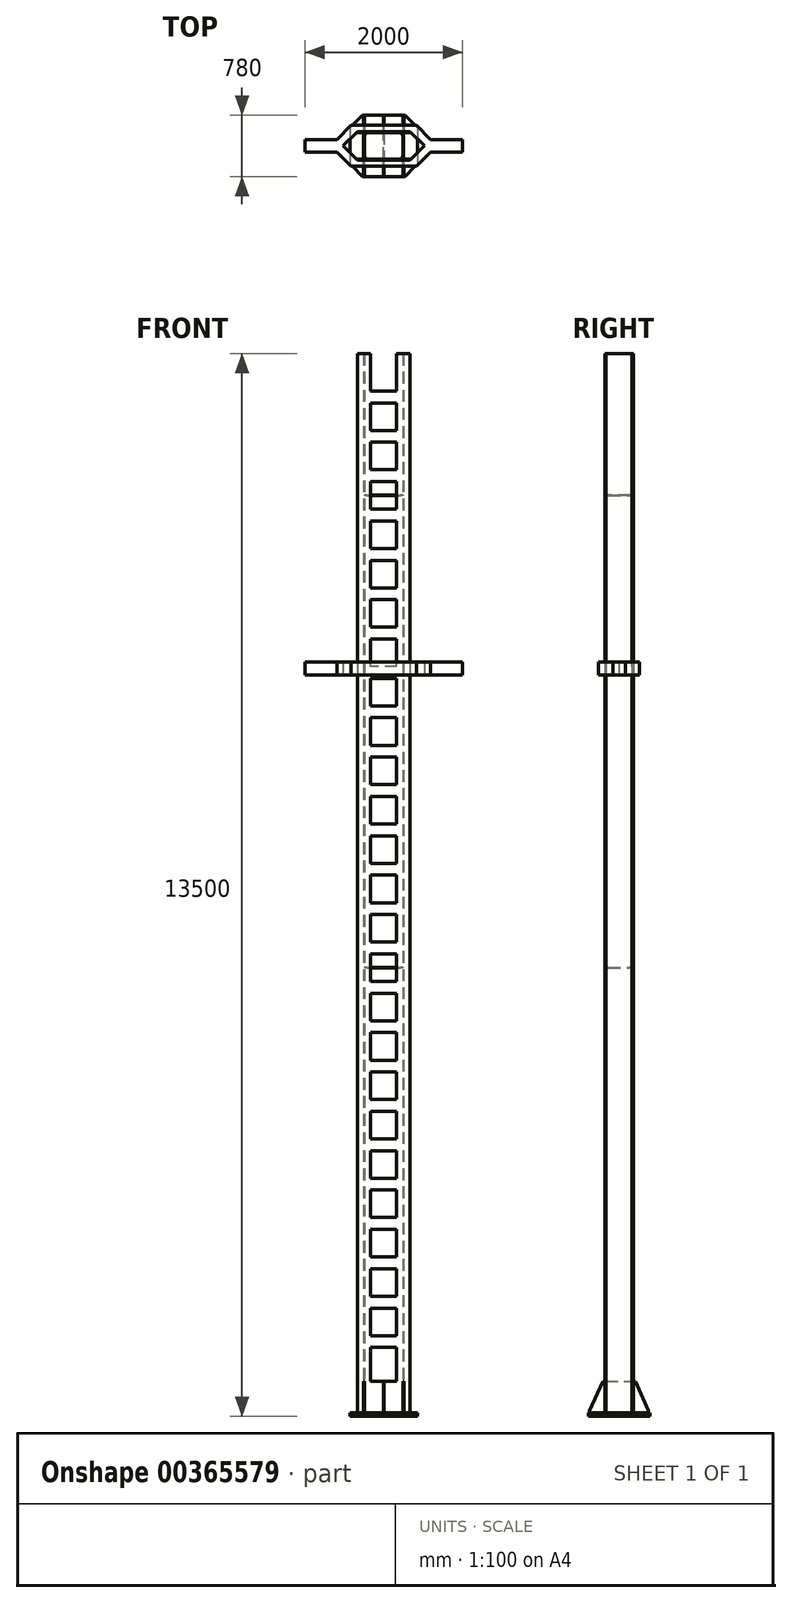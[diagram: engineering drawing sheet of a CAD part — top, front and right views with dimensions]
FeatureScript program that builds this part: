
annotation { "Feature Type Name" : "Feature", "Feature Type Description" : "" }
export const myFeature = defineFeature(function(context is Context, id is Id, definition is map)
    precondition{}
    {
        {
            var Q0;
            Q0=qCreatedBy(makeId("Top.planeOp"),FACE);
            var sketch = newSketch(context, id + "F0", { "sketchPlane" : qUnion([Q0])});
            skLineSegment(sketch, "E0", {"start": v(-335, -180) * mm, "end": v(-335, -166) * mm});
            skLineSegment(sketch, "E1", {"start": v(-335, -166) * mm, "end": v(335, -166) * mm});
            skLineSegment(sketch, "E2", {"start": v(335, -166) * mm, "end": v(335, -180) * mm});
            skLineSegment(sketch, "E3", {"start": v(-335, 180) * mm, "end": v(-335, 166) * mm});
            skLineSegment(sketch, "E4", {"start": v(-335, 166) * mm, "end": v(335, 166) * mm});
            skLineSegment(sketch, "E5", {"start": v(335, 166) * mm, "end": v(335, 180) * mm});
            skLineSegment(sketch, "E6", {"start": v(-246, 166) * mm, "end": v(-246, -166) * mm});
            skLineSegment(sketch, "E7", {"start": v(246, 166) * mm, "end": v(246, -166) * mm});
            skLineSegment(sketch, "E8", {"start": v(-254, -166) * mm, "end": v(-254, 166) * mm});
            skLineSegment(sketch, "E9", {"start": v(254, -166) * mm, "end": v(254, 166) * mm});
            skLineSegment(sketch, "E10", {"start": v(-335, -180) * mm, "end": v(335, -180) * mm});
            skLineSegment(sketch, "E11", {"start": v(-335, 180) * mm, "end": v(335, 180) * mm});
            skSolve(sketch);
        }
        {
            var Q0;
            Q0 = qSketchRegion(id + "F0", true);
            var Q1;
            Q1 = qConstructionFilter(qBodyType(qCreatedBy(id + "F0" ,EDGE), BodyType.WIRE), ConstructionObject.NO);
            extrude(context, id + "F1", {"entities" : qUnion([Q0]), "surfaceEntities" : qUnion([Q1]), "depth" : 13500 * mm});
        }
        {
            var Q0;
            Q0=makeQuery(id+"F1.opExtrude","SWEPT_FACE",FACE,{"disambiguationData":[OSD([sQuery(id+"F0.wireOp",EDGE,"E10")])]});
            var sketch = newSketch(context, id + "F2", { "sketchPlane" : qUnion([Q0])});
            skLineSegment(sketch, "E12.bottom", {"start": v(-165, 13500) * mm, "end": v(165, 13500) * mm});
            skLineSegment(sketch, "E12.top", {"start": v(-165, 13025) * mm, "end": v(165, 13025) * mm});
            skLineSegment(sketch, "E12.left", {"start": v(-165, 13500) * mm, "end": v(-165, 13025) * mm});
            skLineSegment(sketch, "E12.right", {"start": v(165, 13500) * mm, "end": v(165, 13025) * mm});
            skLineSegment(sketch, "E13.bottom", {"start": v(-165, 12875) * mm, "end": v(165, 12875) * mm});
            skLineSegment(sketch, "E13.top", {"start": v(-165, 12525) * mm, "end": v(165, 12525) * mm});
            skLineSegment(sketch, "E13.left", {"start": v(-165, 12875) * mm, "end": v(-165, 12525) * mm});
            skLineSegment(sketch, "E13.right", {"start": v(165, 12875) * mm, "end": v(165, 12525) * mm});
            skLineSegment(sketch, "E14.0.1.0", {"start": v(-165, 12025) * mm, "end": v(165, 12025) * mm});
            skLineSegment(sketch, "E14.0.1.1", {"start": v(165, 12375) * mm, "end": v(165, 12025) * mm});
            skLineSegment(sketch, "E14.0.1.2", {"start": v(-165, 12375) * mm, "end": v(-165, 12025) * mm});
            skLineSegment(sketch, "E14.0.1.3", {"start": v(-165, 12375) * mm, "end": v(165, 12375) * mm});
            skLineSegment(sketch, "E14.0.2.0", {"start": v(-165, 11525) * mm, "end": v(165, 11525) * mm});
            skLineSegment(sketch, "E14.0.2.1", {"start": v(165, 11875) * mm, "end": v(165, 11525) * mm});
            skLineSegment(sketch, "E14.0.2.2", {"start": v(-165, 11875) * mm, "end": v(-165, 11525) * mm});
            skLineSegment(sketch, "E14.0.2.3", {"start": v(-165, 11875) * mm, "end": v(165, 11875) * mm});
            skLineSegment(sketch, "E14.0.3.0", {"start": v(-165, 11025) * mm, "end": v(165, 11025) * mm});
            skLineSegment(sketch, "E14.0.3.1", {"start": v(165, 11375) * mm, "end": v(165, 11025) * mm});
            skLineSegment(sketch, "E14.0.3.2", {"start": v(-165, 11375) * mm, "end": v(-165, 11025) * mm});
            skLineSegment(sketch, "E14.0.3.3", {"start": v(-165, 11375) * mm, "end": v(165, 11375) * mm});
            skLineSegment(sketch, "E14.0.4.0", {"start": v(-165, 10525) * mm, "end": v(165, 10525) * mm});
            skLineSegment(sketch, "E14.0.4.1", {"start": v(165, 10875) * mm, "end": v(165, 10525) * mm});
            skLineSegment(sketch, "E14.0.4.2", {"start": v(-165, 10875) * mm, "end": v(-165, 10525) * mm});
            skLineSegment(sketch, "E14.0.4.3", {"start": v(-165, 10875) * mm, "end": v(165, 10875) * mm});
            skLineSegment(sketch, "E14.0.5.0", {"start": v(-165, 10025) * mm, "end": v(165, 10025) * mm});
            skLineSegment(sketch, "E14.0.5.1", {"start": v(165, 10375) * mm, "end": v(165, 10025) * mm});
            skLineSegment(sketch, "E14.0.5.2", {"start": v(-165, 10375) * mm, "end": v(-165, 10025) * mm});
            skLineSegment(sketch, "E14.0.5.3", {"start": v(-165, 10375) * mm, "end": v(165, 10375) * mm});
            skLineSegment(sketch, "E14.0.6.0", {"start": v(-165, 9525) * mm, "end": v(165, 9525) * mm});
            skLineSegment(sketch, "E14.0.6.1", {"start": v(165, 9875) * mm, "end": v(165, 9525) * mm});
            skLineSegment(sketch, "E14.0.6.2", {"start": v(-165, 9875) * mm, "end": v(-165, 9525) * mm});
            skLineSegment(sketch, "E14.0.6.3", {"start": v(-165, 9875) * mm, "end": v(165, 9875) * mm});
            skLineSegment(sketch, "E14.0.7.0", {"start": v(-165, 9025) * mm, "end": v(165, 9025) * mm});
            skLineSegment(sketch, "E14.0.7.1", {"start": v(165, 9375) * mm, "end": v(165, 9025) * mm});
            skLineSegment(sketch, "E14.0.7.2", {"start": v(-165, 9375) * mm, "end": v(-165, 9025) * mm});
            skLineSegment(sketch, "E14.0.7.3", {"start": v(-165, 9375) * mm, "end": v(165, 9375) * mm});
            skLineSegment(sketch, "E14.0.8.0", {"start": v(-165, 8525) * mm, "end": v(165, 8525) * mm});
            skLineSegment(sketch, "E14.0.8.1", {"start": v(165, 8875) * mm, "end": v(165, 8525) * mm});
            skLineSegment(sketch, "E14.0.8.2", {"start": v(-165, 8875) * mm, "end": v(-165, 8525) * mm});
            skLineSegment(sketch, "E14.0.8.3", {"start": v(-165, 8875) * mm, "end": v(165, 8875) * mm});
            skLineSegment(sketch, "E14.0.9.0", {"start": v(-165, 8025) * mm, "end": v(165, 8025) * mm});
            skLineSegment(sketch, "E14.0.9.1", {"start": v(165, 8375) * mm, "end": v(165, 8025) * mm});
            skLineSegment(sketch, "E14.0.9.2", {"start": v(-165, 8375) * mm, "end": v(-165, 8025) * mm});
            skLineSegment(sketch, "E14.0.9.3", {"start": v(-165, 8375) * mm, "end": v(165, 8375) * mm});
            skLineSegment(sketch, "E14.0.10.0", {"start": v(-165, 7525) * mm, "end": v(165, 7525) * mm});
            skLineSegment(sketch, "E14.0.10.1", {"start": v(165, 7875) * mm, "end": v(165, 7525) * mm});
            skLineSegment(sketch, "E14.0.10.2", {"start": v(-165, 7875) * mm, "end": v(-165, 7525) * mm});
            skLineSegment(sketch, "E14.0.10.3", {"start": v(-165, 7875) * mm, "end": v(165, 7875) * mm});
            skLineSegment(sketch, "E14.0.11.0", {"start": v(-165, 7025) * mm, "end": v(165, 7025) * mm});
            skLineSegment(sketch, "E14.0.11.1", {"start": v(165, 7375) * mm, "end": v(165, 7025) * mm});
            skLineSegment(sketch, "E14.0.11.2", {"start": v(-165, 7375) * mm, "end": v(-165, 7025) * mm});
            skLineSegment(sketch, "E14.0.11.3", {"start": v(-165, 7375) * mm, "end": v(165, 7375) * mm});
            skLineSegment(sketch, "E14.0.12.0", {"start": v(-165, 6525) * mm, "end": v(165, 6525) * mm});
            skLineSegment(sketch, "E14.0.12.1", {"start": v(165, 6875) * mm, "end": v(165, 6525) * mm});
            skLineSegment(sketch, "E14.0.12.2", {"start": v(-165, 6875) * mm, "end": v(-165, 6525) * mm});
            skLineSegment(sketch, "E14.0.12.3", {"start": v(-165, 6875) * mm, "end": v(165, 6875) * mm});
            skLineSegment(sketch, "E14.0.13.0", {"start": v(-165, 6025) * mm, "end": v(165, 6025) * mm});
            skLineSegment(sketch, "E14.0.13.1", {"start": v(165, 6375) * mm, "end": v(165, 6025) * mm});
            skLineSegment(sketch, "E14.0.13.2", {"start": v(-165, 6375) * mm, "end": v(-165, 6025) * mm});
            skLineSegment(sketch, "E14.0.13.3", {"start": v(-165, 6375) * mm, "end": v(165, 6375) * mm});
            skLineSegment(sketch, "E14.0.14.0", {"start": v(-165, 5525) * mm, "end": v(165, 5525) * mm});
            skLineSegment(sketch, "E14.0.14.1", {"start": v(165, 5875) * mm, "end": v(165, 5525) * mm});
            skLineSegment(sketch, "E14.0.14.2", {"start": v(-165, 5875) * mm, "end": v(-165, 5525) * mm});
            skLineSegment(sketch, "E14.0.14.3", {"start": v(-165, 5875) * mm, "end": v(165, 5875) * mm});
            skLineSegment(sketch, "E14.0.15.0", {"start": v(-165, 5025) * mm, "end": v(165, 5025) * mm});
            skLineSegment(sketch, "E14.0.15.1", {"start": v(165, 5375) * mm, "end": v(165, 5025) * mm});
            skLineSegment(sketch, "E14.0.15.2", {"start": v(-165, 5375) * mm, "end": v(-165, 5025) * mm});
            skLineSegment(sketch, "E14.0.15.3", {"start": v(-165, 5375) * mm, "end": v(165, 5375) * mm});
            skLineSegment(sketch, "E14.0.16.0", {"start": v(-165, 4525) * mm, "end": v(165, 4525) * mm});
            skLineSegment(sketch, "E14.0.16.1", {"start": v(165, 4875) * mm, "end": v(165, 4525) * mm});
            skLineSegment(sketch, "E14.0.16.2", {"start": v(-165, 4875) * mm, "end": v(-165, 4525) * mm});
            skLineSegment(sketch, "E14.0.16.3", {"start": v(-165, 4875) * mm, "end": v(165, 4875) * mm});
            skLineSegment(sketch, "E14.0.17.0", {"start": v(-165, 4025) * mm, "end": v(165, 4025) * mm});
            skLineSegment(sketch, "E14.0.17.1", {"start": v(165, 4375) * mm, "end": v(165, 4025) * mm});
            skLineSegment(sketch, "E14.0.17.2", {"start": v(-165, 4375) * mm, "end": v(-165, 4025) * mm});
            skLineSegment(sketch, "E14.0.17.3", {"start": v(-165, 4375) * mm, "end": v(165, 4375) * mm});
            skLineSegment(sketch, "E14.0.18.0", {"start": v(-165, 3525) * mm, "end": v(165, 3525) * mm});
            skLineSegment(sketch, "E14.0.18.1", {"start": v(165, 3875) * mm, "end": v(165, 3525) * mm});
            skLineSegment(sketch, "E14.0.18.2", {"start": v(-165, 3875) * mm, "end": v(-165, 3525) * mm});
            skLineSegment(sketch, "E14.0.18.3", {"start": v(-165, 3875) * mm, "end": v(165, 3875) * mm});
            skLineSegment(sketch, "E14.0.19.0", {"start": v(-165, 3025) * mm, "end": v(165, 3025) * mm});
            skLineSegment(sketch, "E14.0.19.1", {"start": v(165, 3375) * mm, "end": v(165, 3025) * mm});
            skLineSegment(sketch, "E14.0.19.2", {"start": v(-165, 3375) * mm, "end": v(-165, 3025) * mm});
            skLineSegment(sketch, "E14.0.19.3", {"start": v(-165, 3375) * mm, "end": v(165, 3375) * mm});
            skLineSegment(sketch, "E14.direction1", {"start": v(-165, 12525) * mm, "end": v(-140, 12525) * mm, "construction": true});
            skLineSegment(sketch, "E14.direction2", {"start": v(-165, 12525) * mm, "end": v(-165, 12025) * mm, "construction": true});
            skLineSegment(sketch, "E15.0.0.20", {"start": v(-165, 2525) * mm, "end": v(165, 2525) * mm});
            skLineSegment(sketch, "E15.3.0.20", {"start": v(165, 2875) * mm, "end": v(165, 2525) * mm});
            skLineSegment(sketch, "E15.6.0.20", {"start": v(-165, 2875) * mm, "end": v(-165, 2525) * mm});
            skLineSegment(sketch, "E15.9.0.20", {"start": v(-165, 2875) * mm, "end": v(165, 2875) * mm});
            skLineSegment(sketch, "E15.0.0.21", {"start": v(-165, 2025) * mm, "end": v(165, 2025) * mm});
            skLineSegment(sketch, "E15.3.0.21", {"start": v(165, 2375) * mm, "end": v(165, 2025) * mm});
            skLineSegment(sketch, "E15.6.0.21", {"start": v(-165, 2375) * mm, "end": v(-165, 2025) * mm});
            skLineSegment(sketch, "E15.9.0.21", {"start": v(-165, 2375) * mm, "end": v(165, 2375) * mm});
            skLineSegment(sketch, "E15.0.0.22", {"start": v(-165, 1525) * mm, "end": v(165, 1525) * mm});
            skLineSegment(sketch, "E15.3.0.22", {"start": v(165, 1875) * mm, "end": v(165, 1525) * mm});
            skLineSegment(sketch, "E15.6.0.22", {"start": v(-165, 1875) * mm, "end": v(-165, 1525) * mm});
            skLineSegment(sketch, "E15.9.0.22", {"start": v(-165, 1875) * mm, "end": v(165, 1875) * mm});
            skLineSegment(sketch, "E15.0.0.23", {"start": v(-165, 1025) * mm, "end": v(165, 1025) * mm});
            skLineSegment(sketch, "E15.3.0.23", {"start": v(165, 1375) * mm, "end": v(165, 1025) * mm});
            skLineSegment(sketch, "E15.6.0.23", {"start": v(-165, 1375) * mm, "end": v(-165, 1025) * mm});
            skLineSegment(sketch, "E15.9.0.23", {"start": v(-165, 1375) * mm, "end": v(165, 1375) * mm});
            skLineSegment(sketch, "E16.bottom", {"start": v(165, 875) * mm, "end": v(-165, 875) * mm});
            skLineSegment(sketch, "E16.top", {"start": v(165, 445) * mm, "end": v(-165, 445) * mm});
            skLineSegment(sketch, "E16.left", {"start": v(165, 875) * mm, "end": v(165, 445) * mm});
            skLineSegment(sketch, "E16.right", {"start": v(-165, 875) * mm, "end": v(-165, 445) * mm});
            skSolve(sketch);
        }
        {
            var Q0;
            Q0 = qSketchRegion(id + "F2", true);
            extrude(context, id + "F3", {"entities" : qUnion([Q0]), "operationType" : NewBodyOperationType.REMOVE, "endBound" : BoundingType.THROUGH_ALL, "oppositeDirection" : true, "depth" : 25 * mm});
        }
        {
            var Q0;
            {var subQ0=sQuery(id+"F0.wireOp",EDGE,"E6");Q0=makeQuery(id+"F0.imprint","IMPRINT",FACE,{"disambiguationData":[TD([[makeQuery(id+"F0.imprint","IMPRINT",EDGE,{"derivedFrom":subQ0}),1.0]])]});}
            var sketch = newSketch(context, id + "F4", { "sketchPlane" : qUnion([Q0])});
            skLineSegment(sketch, "E17.bottom", {"start": v(-270, 390) * mm, "end": v(270, 390) * mm});
            skLineSegment(sketch, "E17.top", {"start": v(-270, -390) * mm, "end": v(270, -390) * mm});
            skLineSegment(sketch, "E17.left", {"start": v(-430, 230) * mm, "end": v(-430, -230) * mm});
            skLineSegment(sketch, "E17.right", {"start": v(430, 230) * mm, "end": v(430, -230) * mm});
            skLineSegment(sketch, "E18", {"start": v(270, -390) * mm, "end": v(430, -230) * mm});
            skLineSegment(sketch, "E19", {"start": v(430, 230) * mm, "end": v(270, 390) * mm});
            skLineSegment(sketch, "E20", {"start": v(-270, 390) * mm, "end": v(-430, 230) * mm});
            skLineSegment(sketch, "E21", {"start": v(-270, -390) * mm, "end": v(-430, -230) * mm});
            skSolve(sketch);
        }
        {
            var Q0;
            Q0 = qSketchRegion(id + "F4", true);
            extrude(context, id + "F5", {"entities" : qUnion([Q0]), "operationType" : NewBodyOperationType.ADD, "depth" : 45 * mm});
        }
        {
            var Q0;
            Q0=qCreatedBy(makeId("Right.planeOp"),FACE);
            var sketch = newSketch(context, id + "F6", { "sketchPlane" : qUnion([Q0])});
            skLineSegment(sketch, "E22", {"start": v(-205, 445) * mm, "end": v(205, 445) * mm});
            skLineSegment(sketch, "E23", {"start": v(205, 445) * mm, "end": v(375, 70) * mm});
            skLineSegment(sketch, "E24", {"start": v(375, 70) * mm, "end": v(375, 45) * mm});
            skLineSegment(sketch, "E25", {"start": v(375, 45) * mm, "end": v(-375, 45) * mm});
            skLineSegment(sketch, "E26", {"start": v(-375, 45) * mm, "end": v(-375, 70) * mm});
            skLineSegment(sketch, "E27", {"start": v(-375, 70) * mm, "end": v(-205, 445) * mm});
            skSolve(sketch);
        }
        {
            var Q0;
            Q0 = qSketchRegion(id + "F6", true);
            var Q1;
            Q1 = qConstructionFilter(qBodyType(qCreatedBy(id + "F6" ,EDGE), BodyType.WIRE), ConstructionObject.NO);
            extrude(context, id + "F7", {"entities" : qUnion([Q0]), "operationType" : NewBodyOperationType.ADD, "surfaceEntities" : qUnion([Q1]), "endBound" : BoundingType.SYMMETRIC, "depth" : 12 * mm});
        }
        {
            var Q0;
            Q0=qCreatedBy(makeId("Front.planeOp"),FACE);
            var sketch = newSketch(context, id + "F8", { "sketchPlane" : qUnion([Q0])});
            skLineSegment(sketch, "E28", {"start": v(0, 0) * mm, "end": v(0, 479.8) * mm});
            skSolve(sketch);
        }
        {
            var Q0;
            Q0=qCreatedBy(makeId("Right.planeOp"),FACE);
            cPlane(context, id + "F9", {"entities" : qUnion([Q0]), "cplaneType" : CPlaneType.OFFSET, "offset" : 250 * mm, "width" : 150 * mm, "height" : 150 * mm});
        }
        {
            var Q0;
            Q0=qCreatedBy(id+"F9.planeOp",FACE);
            var sketch = newSketch(context, id + "F10", { "sketchPlane" : qUnion([Q0])});
            skLineSegment(sketch, "E29", {"start": v(-375, 45) * mm, "end": v(-375, 70) * mm});
            skLineSegment(sketch, "E30", {"start": v(-375, 70) * mm, "end": v(-205, 445) * mm});
            skLineSegment(sketch, "E31", {"start": v(-205, 445) * mm, "end": v(-180, 445) * mm});
            skLineSegment(sketch, "E32", {"start": v(-180, 445) * mm, "end": v(-180, 45) * mm});
            skLineSegment(sketch, "E33", {"start": v(-180, 45) * mm, "end": v(-375, 45) * mm});
            skLineSegment(sketch, "E34.MirrorCS", {"start": v(205, 445) * mm, "end": v(180, 445) * mm});
            skLineSegment(sketch, "E35.MirrorCS", {"start": v(375, 70) * mm, "end": v(205, 445) * mm});
            skLineSegment(sketch, "E36.MirrorCS", {"start": v(180, 445) * mm, "end": v(180, 45) * mm});
            skLineSegment(sketch, "E37.MirrorCS", {"start": v(180, 45) * mm, "end": v(375, 45) * mm});
            skLineSegment(sketch, "E38.MirrorCS", {"start": v(375, 45) * mm, "end": v(375, 70) * mm});
            skSolve(sketch);
        }
        {
            var Q0;
            Q0 = qSketchRegion(id + "F10", true);
            extrude(context, id + "F11", {"entities" : qUnion([Q0]), "operationType" : NewBodyOperationType.ADD, "endBound" : BoundingType.SYMMETRIC, "depth" : 14 * mm});
        }
        {
            var Q0;
            Q0=qCreatedBy(makeId("Right.planeOp"),FACE);
            cPlane(context, id + "F12", {"entities" : qUnion([Q0]), "cplaneType" : CPlaneType.OFFSET, "offset" : 250 * mm, "oppositeDirection" : true, "width" : 150 * mm, "height" : 150 * mm});
        }
        {
            var Q0;
            Q0=qCreatedBy(id+"F12.planeOp",FACE);
            var sketch = newSketch(context, id + "F13", { "sketchPlane" : qUnion([Q0])});
            skLineSegment(sketch, "E39", {"start": v(375, 45) * mm, "end": v(375, 70) * mm});
            skLineSegment(sketch, "E40", {"start": v(375, 70) * mm, "end": v(205, 445) * mm});
            skLineSegment(sketch, "E41", {"start": v(205, 445) * mm, "end": v(180, 445) * mm});
            skLineSegment(sketch, "E42", {"start": v(180, 445) * mm, "end": v(180, 45) * mm});
            skLineSegment(sketch, "E43", {"start": v(180, 45) * mm, "end": v(375, 45) * mm});
            skLineSegment(sketch, "E44.MirrorCS", {"start": v(-205, 445) * mm, "end": v(-180, 445) * mm});
            skLineSegment(sketch, "E45.MirrorCS", {"start": v(-375, 70) * mm, "end": v(-205, 445) * mm});
            skLineSegment(sketch, "E46.MirrorCS", {"start": v(-180, 445) * mm, "end": v(-180, 45) * mm});
            skLineSegment(sketch, "E47.MirrorCS", {"start": v(-180, 45) * mm, "end": v(-375, 45) * mm});
            skLineSegment(sketch, "E48.MirrorCS", {"start": v(-375, 45) * mm, "end": v(-375, 70) * mm});
            skSolve(sketch);
        }
        {
            var Q0;
            Q0 = qSketchRegion(id + "F13", true);
            extrude(context, id + "F14", {"entities" : qUnion([Q0]), "operationType" : NewBodyOperationType.ADD, "endBound" : BoundingType.SYMMETRIC, "depth" : 14 * mm});
        }
        {
            var Q0;
            {var subQ0=sQuery(id+"F0.wireOp",EDGE,"E6");Q0=makeQuery(id+"F0.imprint","IMPRINT",FACE,{"disambiguationData":[TD([[makeQuery(id+"F0.imprint","IMPRINT",EDGE,{"derivedFrom":subQ0}),1.0]])]});}
            cPlane(context, id + "F15", {"entities" : qUnion([Q0]), "cplaneType" : CPlaneType.OFFSET, "offset" : 5700 * mm, "width" : 150 * mm, "height" : 150 * mm});
        }
        {
            var Q0;
            Q0=qCreatedBy(id+"F15.planeOp",FACE);
            var sketch = newSketch(context, id + "F16", { "sketchPlane" : qUnion([Q0])});
            skLineSegment(sketch, "E49", {"start": v(-211, -167.5) * mm, "end": v(211, -167.5) * mm});
            skLineSegment(sketch, "E50", {"start": v(211, -167.5) * mm, "end": v(246, -132.5) * mm});
            skLineSegment(sketch, "E51", {"start": v(246, -132.5) * mm, "end": v(246, 132.5) * mm});
            skLineSegment(sketch, "E52", {"start": v(246, 132.5) * mm, "end": v(211, 167.5) * mm});
            skLineSegment(sketch, "E53", {"start": v(211, 167.5) * mm, "end": v(-211, 167.5) * mm});
            skLineSegment(sketch, "E54", {"start": v(-211, 167.5) * mm, "end": v(-246, 132.5) * mm});
            skLineSegment(sketch, "E55", {"start": v(-246, 132.5) * mm, "end": v(-246, -132.5) * mm});
            skLineSegment(sketch, "E56", {"start": v(-246, -132.5) * mm, "end": v(-211, -167.5) * mm});
            skSolve(sketch);
        }
        {
            var Q0;
            Q0 = qSketchRegion(id + "F16", true);
            extrude(context, id + "F17", {"entities" : qUnion([Q0]), "operationType" : NewBodyOperationType.ADD, "endBound" : BoundingType.SYMMETRIC, "depth" : 6 * mm});
        }
        {
            var Q0;
            Q0=qCreatedBy(id+"F15.planeOp",FACE);
            cPlane(context, id + "F18", {"entities" : qUnion([Q0]), "cplaneType" : CPlaneType.OFFSET, "offset" : 6000 * mm, "width" : 150 * mm, "height" : 150 * mm});
        }
        {
            var Q0;
            Q0=qCreatedBy(id+"F18.planeOp",FACE);
            var sketch = newSketch(context, id + "F19", { "sketchPlane" : qUnion([Q0])});
            skLineSegment(sketch, "E57", {"start": v(-215, -167.5) * mm, "end": v(211, -167.5) * mm});
            skLineSegment(sketch, "E58", {"start": v(211, -167.5) * mm, "end": v(246, -132.5) * mm});
            skLineSegment(sketch, "E59", {"start": v(246, -132.5) * mm, "end": v(246, 132.5) * mm});
            skLineSegment(sketch, "E60", {"start": v(246, 132.5) * mm, "end": v(211, 167.5) * mm});
            skLineSegment(sketch, "E61", {"start": v(211, 167.5) * mm, "end": v(-215, 167.5) * mm});
            skLineSegment(sketch, "E62", {"start": v(-215, 167.5) * mm, "end": v(-250, 132.5) * mm});
            skLineSegment(sketch, "E63", {"start": v(-250, 132.5) * mm, "end": v(-250, -132.5) * mm});
            skLineSegment(sketch, "E64", {"start": v(-250, -132.5) * mm, "end": v(-215, -167.5) * mm});
            skSolve(sketch);
        }
        {
            var Q0;
            Q0 = qSketchRegion(id + "F19", true);
            extrude(context, id + "F20", {"entities" : qUnion([Q0]), "operationType" : NewBodyOperationType.ADD, "endBound" : BoundingType.SYMMETRIC, "depth" : 6 * mm});
        }
        {
            var Q0;
            Q0=qCreatedBy(makeId("Top.planeOp"),FACE);
            cPlane(context, id + "F21", {"entities" : qUnion([Q0]), "cplaneType" : CPlaneType.OFFSET, "offset" : 9500 * mm, "width" : 150 * mm, "height" : 150 * mm});
        }
        {
            var Q0;
            Q0=qCreatedBy(id+"F21.planeOp",FACE);
            var sketch = newSketch(context, id + "F22", { "sketchPlane" : qUnion([Q0])});
            skLineSegment(sketch, "E65", {"start": v(-335, 180) * mm, "end": v(335, 180) * mm});
            skLineSegment(sketch, "E66", {"start": v(335, 180) * mm, "end": v(515, 0) * mm});
            skLineSegment(sketch, "E67", {"start": v(515, 0) * mm, "end": v(335, -180) * mm});
            skLineSegment(sketch, "E68", {"start": v(335, -180) * mm, "end": v(-335, -180) * mm});
            skLineSegment(sketch, "E69", {"start": v(-335, -180) * mm, "end": v(-515, 0) * mm});
            skLineSegment(sketch, "E70", {"start": v(-515, 0) * mm, "end": v(-335, 180) * mm});
            skLineSegment(sketch, "E71", {"start": v(-416, 261) * mm, "end": v(416, 261) * mm});
            skLineSegment(sketch, "E72", {"start": v(416, 261) * mm, "end": v(596, 81) * mm});
            skLineSegment(sketch, "E73", {"start": v(596, 81) * mm, "end": v(1000, 81) * mm});
            skLineSegment(sketch, "E74", {"start": v(596, -81) * mm, "end": v(416, -261) * mm});
            skLineSegment(sketch, "E75", {"start": v(416, -261) * mm, "end": v(-416, -261) * mm});
            skLineSegment(sketch, "E76", {"start": v(-416, -261) * mm, "end": v(-596, -81) * mm});
            skLineSegment(sketch, "E77", {"start": v(-596, -81) * mm, "end": v(-1000, -81) * mm});
            skLineSegment(sketch, "E78", {"start": v(-1000, -81) * mm, "end": v(-1000, 81) * mm});
            skLineSegment(sketch, "E79", {"start": v(-1000, 81) * mm, "end": v(-596, 81) * mm});
            skLineSegment(sketch, "E80", {"start": v(-596, 81) * mm, "end": v(-416, 261) * mm});
            skLineSegment(sketch, "E81", {"start": v(1000, 81) * mm, "end": v(1000, -81) * mm});
            skLineSegment(sketch, "E82", {"start": v(1000, -81) * mm, "end": v(596, -81) * mm});
            skSolve(sketch);
        }
        {
            var Q0;
            Q0 = qSketchRegion(id + "F22", true);
            extrude(context, id + "F23", {"entities" : qUnion([Q0]), "operationType" : NewBodyOperationType.ADD, "endBound" : BoundingType.SYMMETRIC, "depth" : 162 * mm});
        }
    });
